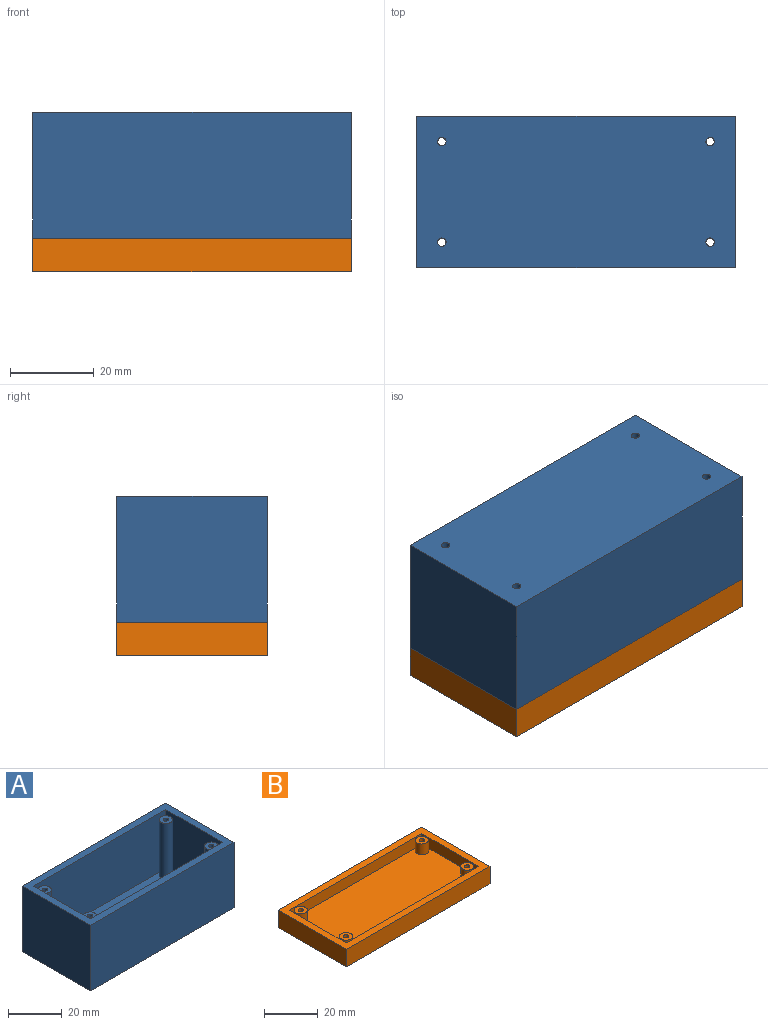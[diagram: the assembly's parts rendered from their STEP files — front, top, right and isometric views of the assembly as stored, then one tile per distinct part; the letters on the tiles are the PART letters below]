
ASSEMBLY  parts=2 mates=1
PART A: 23 faces, bbox 76x36x30 mm
  f0: plane 76x36mm, normal (0,0,1), area 636mm2, adj f1,f2,f3,f4,f6,f7,f8,f9
  f1: plane 36x30mm, normal (1,0,0), area 1080mm2, adj f0,f2,f4,f5
  f2: plane 76x30mm, normal (0,1,0), area 2280mm2, adj f0,f1,f3,f5
  f3: plane 36x30mm, normal (-1,0,0), area 1080mm2, adj f0,f2,f4,f5
  f4: plane 76x30mm, normal (0,-1,0), area 2280mm2, adj f0,f1,f3,f5
  f5: plane 76x36mm, normal (0,0,-1), area 2723.4mm2, adj f1,f2,f3,f4,f12,f15,f17,f20
  f6: plane 30x27mm, normal (-1,0,0), area 810mm2, adj f0,f7,f9,f10
  f7: plane 70x27mm, normal (0,-1,0), area 1890mm2, adj f0,f6,f8,f10
  f8: plane 30x27mm, normal (1,0,0), area 810mm2, adj f0,f7,f9,f10
  f9: plane 70x27mm, normal (0,1,0), area 1890mm2, adj f0,f6,f8,f10
  f10: plane 70x30mm, normal (0,0,1), area 2021.5mm2, adj f6,f7,f8,f9,f11,f14,f18,f21
  f11: cylinder r=2.5mm len=25.4mm, axis (0,0,-1), area 399mm2, adj f10,f13
  f12: cylinder r=1mm len=28.4mm, axis (0,0,-1), area 178.4mm2, adj f5,f13
  f13: plane 5x5mm, normal (0,0,1), area 16.5mm2, adj f11,f12
  f14: cylinder r=2.5mm len=25.4mm, axis (0,0,-1), area 399mm2, adj f10,f16
  f15: cylinder r=1mm len=28.4mm, axis (0,0,-1), area 178.4mm2, adj f5,f16
  f16: plane 5x5mm, normal (0,0,1), area 16.5mm2, adj f14,f15
  f17: cylinder r=1mm len=28.4mm, axis (0,0,-1), area 178.4mm2, adj f5,f19
  f18: cylinder r=2.5mm len=25.4mm, axis (0,0,-1), area 399mm2, adj f10,f19
  f19: plane 5x5mm, normal (0,0,1), area 16.5mm2, adj f17,f18
  f20: cylinder r=1mm len=28.4mm, axis (0,0,-1), area 178.4mm2, adj f5,f22
  f21: cylinder r=2.5mm len=25.4mm, axis (0,0,-1), area 399mm2, adj f10,f22
  f22: plane 5x5mm, normal (0,0,1), area 16.5mm2, adj f20,f21
PART B: 23 faces, bbox 76x36x8 mm
  f0: plane 70x30mm, normal (0,0,1), area 2021.5mm2, adj f10,f11,f12,f13,f15,f17,f19,f21
  f1: plane 76x8mm, normal (0,1,0), area 608mm2, adj f2,f7,f9,f14
  f2: plane 36x8mm, normal (-1,0,0), area 288mm2, adj f1,f3,f9,f14
  f3: plane 76x8mm, normal (0,-1,0), area 608mm2, adj f2,f7,f9,f14
  f4: cylinder r=1mm len=8mm, axis (0,0,-1), area 50.3mm2, adj f9,f20
  f5: cylinder r=1mm len=8mm, axis (0,0,-1), area 50.3mm2, adj f9,f18
  f6: cylinder r=1mm len=8mm, axis (0,0,-1), area 50.3mm2, adj f9,f16
  f7: plane 36x8mm, normal (1,0,0), area 288mm2, adj f1,f3,f9,f14
  f8: cylinder r=1mm len=8mm, axis (0,0,-1), area 50.3mm2, adj f9,f22
  f9: plane 76x36mm, normal (0,0,-1), area 2723.4mm2, adj f1,f2,f3,f4,f5,f6,f7,f8
  f10: plane 70x5mm, normal (0,-1,0), area 350mm2, adj f0,f11,f13,f14
  f11: plane 30x5mm, normal (-1,0,0), area 150mm2, adj f0,f10,f12,f14
  f12: plane 70x5mm, normal (0,1,0), area 350mm2, adj f0,f11,f13,f14
  f13: plane 30x5mm, normal (1,0,0), area 150mm2, adj f0,f10,f12,f14
  f14: plane 76x36mm, normal (0,0,1), area 636mm2, adj f1,f2,f3,f7,f10,f11,f12,f13
  f15: cylinder r=2.5mm len=5mm, axis (0,0,-1), area 78.5mm2, adj f0,f16
  f16: plane 5x5mm, normal (0,0,1), area 16.5mm2, adj f6,f15
  f17: cylinder r=2.5mm len=5mm, axis (0,0,-1), area 78.5mm2, adj f0,f18
  f18: plane 5x5mm, normal (0,0,1), area 16.5mm2, adj f5,f17
  f19: cylinder r=2.5mm len=5mm, axis (0,0,-1), area 78.5mm2, adj f0,f20
  f20: plane 5x5mm, normal (0,0,1), area 16.5mm2, adj f4,f19
  f21: cylinder r=2.5mm len=5mm, axis (0,0,-1), area 78.5mm2, adj f0,f22
  f22: plane 5x5mm, normal (0,0,1), area 16.5mm2, adj f8,f21
PLACE A rot(axis=(0,1,0),180deg) t=(-1.11,5.81,41.96)mm
PLACE B rot(axis=(0,-1,0),0deg) t=(-1.11,5.81,3.96)mm
MATE fastened B.f14 <-> A.f0  axis (0,0,1) through (-1.11,5.81,11.96)mm
